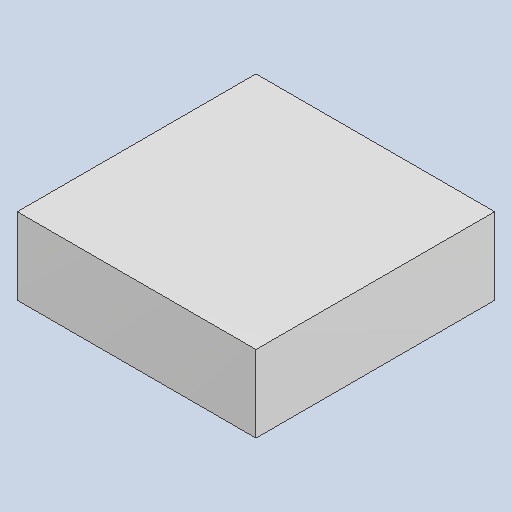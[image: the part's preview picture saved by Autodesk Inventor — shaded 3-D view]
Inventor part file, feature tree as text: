
AUTODESK INVENTOR PART (.ipt)
format: ipt  version: 2023.4 (Build 274418000, 418)  size: 79,872 bytes
history: native  units: mm
features: extrude x1
ambient origin geometry x8: Origin, YZ Plane, XZ Plane, XY Plane, X Axis, Y Axis, Z Axis, Center Point
bodies: Solid1 (feature_tree)
feature tree (1):
  extrude  "Extruded_17"  [1 undecoded]
note: 1 required parameter value undecoded (feature->parameter linkage not recoverable at this tier; creation-order binding heuristic only, values carry confidence <= 0.55)
